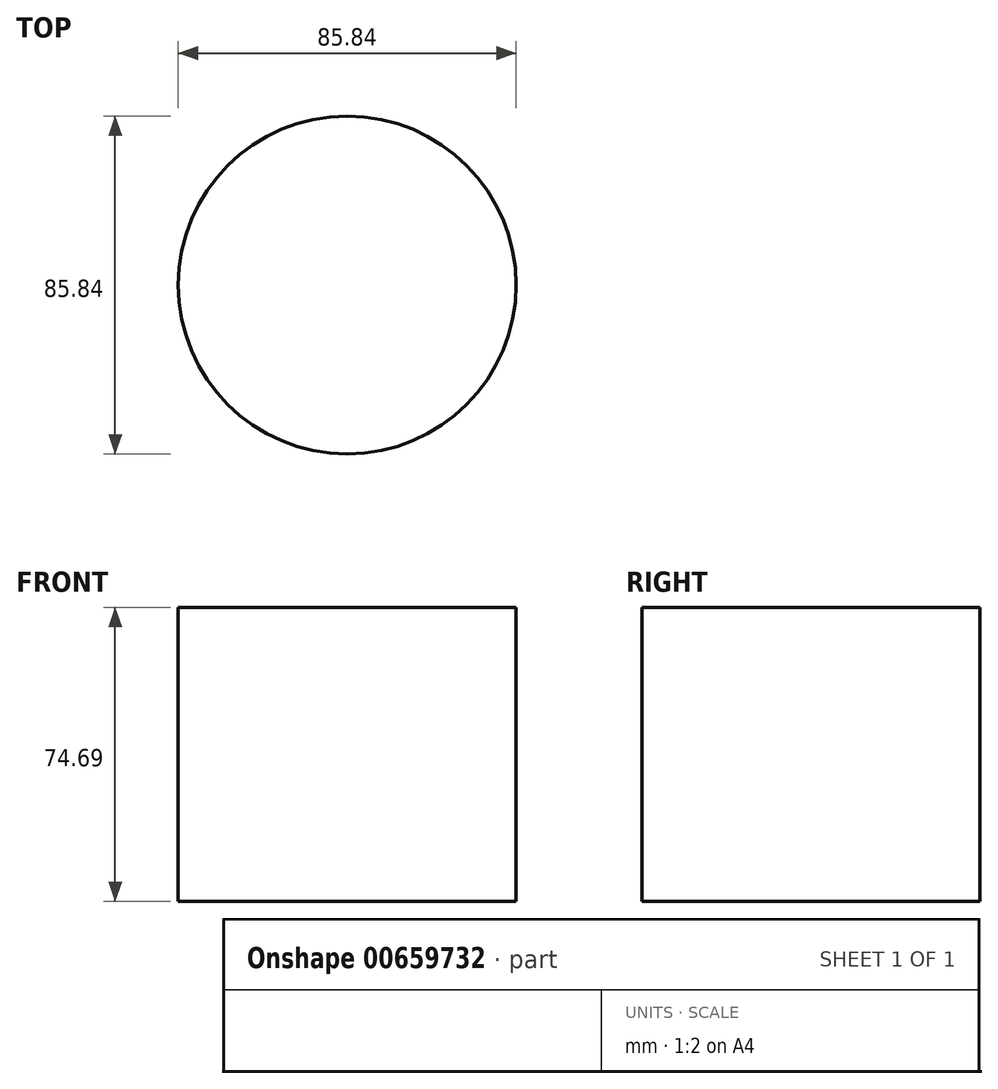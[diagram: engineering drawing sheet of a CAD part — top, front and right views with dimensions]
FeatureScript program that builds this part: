
annotation { "Feature Type Name" : "Feature", "Feature Type Description" : "" }
export const myFeature = defineFeature(function(context is Context, id is Id, definition is map)
    precondition{}
    {
        {
            var Q0;
            Q0=qCreatedBy(makeId("Top.planeOp"),FACE);
            var sketch = newSketch(context, id + "F0", { "sketchPlane" : qUnion([Q0])});
            skCircle(sketch, "E0", {"center": v(-8.76, 22.86) * mm, "radius": 42.92 * mm});
            skSolve(sketch);
        }
        {
            var Q0;
            Q0=makeQuery(id+"F0.imprint","IMPRINT",FACE,{"disambiguationData":[TD([[makeQuery(id+"F0.imprint","IMPRINT",EDGE,{"derivedFrom":sQuery(id+"F0.wireOp",EDGE,"E0")}),1.0]])]});
            extrude(context, id + "F1", {"entities" : qUnion([Q0]), "oppositeDirection" : true, "depth" : 74.69 * mm, "offsetDistance" : 25 * mm});
        }
    });
